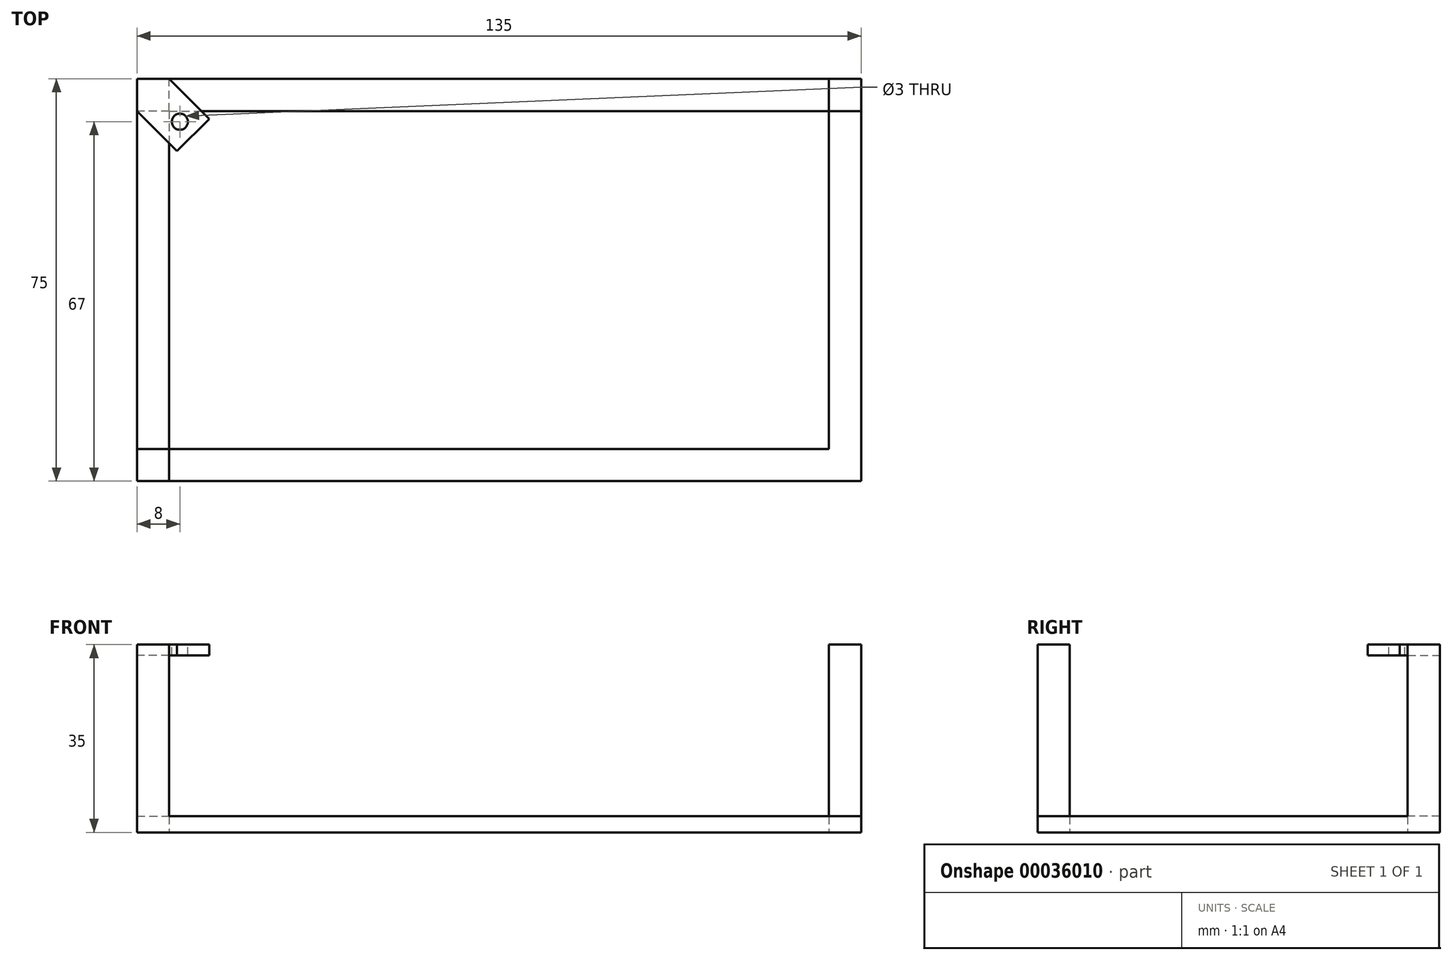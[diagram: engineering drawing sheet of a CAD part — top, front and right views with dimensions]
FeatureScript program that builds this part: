
annotation { "Feature Type Name" : "Feature", "Feature Type Description" : "" }
export const myFeature = defineFeature(function(context is Context, id is Id, definition is map)
    precondition{}
    {
        {
            var Q0;
            Q0=qCreatedBy(makeId("Top.planeOp"),FACE);
            var sketch = newSketch(context, id + "F0", { "sketchPlane" : qUnion([Q0])});
            skLineSegment(sketch, "E0.rect.bottom", {"start": v(-67.5, 37.5) * mm, "end": v(67.5, 37.5) * mm});
            skLineSegment(sketch, "E0.rect.top", {"start": v(-67.5, -37.5) * mm, "end": v(67.5, -37.5) * mm});
            skLineSegment(sketch, "E0.rect.left", {"start": v(-67.5, 37.5) * mm, "end": v(-67.5, -37.5) * mm});
            skLineSegment(sketch, "E0.rect.right", {"start": v(67.5, 37.5) * mm, "end": v(67.5, -37.5) * mm});
            skPoint(sketch, "E0.rect.middle", {"position": v(0, 0) * mm});
            skLineSegment(sketch, "E1.0", {"start": v(-61.5, 31.5) * mm, "end": v(61.5, 31.5) * mm});
            skLineSegment(sketch, "E1.1", {"start": v(-61.5, 31.5) * mm, "end": v(-61.5, -31.5) * mm});
            skLineSegment(sketch, "E1.2", {"start": v(-61.5, -31.5) * mm, "end": v(61.5, -31.5) * mm});
            skLineSegment(sketch, "E1.3", {"start": v(61.5, 31.5) * mm, "end": v(61.5, -31.5) * mm});
            skLineSegment(sketch, "E2.bottom", {"start": v(-61.5, 31.5) * mm, "end": v(-67.5, 31.5) * mm});
            skLineSegment(sketch, "E2.top", {"start": v(-61.5, 37.5) * mm, "end": v(-67.5, 37.5) * mm});
            skLineSegment(sketch, "E2.left", {"start": v(-61.5, 31.5) * mm, "end": v(-61.5, 37.5) * mm});
            skLineSegment(sketch, "E2.right", {"start": v(-67.5, 31.5) * mm, "end": v(-67.5, 37.5) * mm});
            skLineSegment(sketch, "E3.bottom", {"start": v(-61.5, -31.5) * mm, "end": v(-67.5, -31.5) * mm});
            skLineSegment(sketch, "E3.top", {"start": v(-61.5, -37.5) * mm, "end": v(-67.5, -37.5) * mm});
            skLineSegment(sketch, "E3.left", {"start": v(-61.5, -31.5) * mm, "end": v(-61.5, -37.5) * mm});
            skLineSegment(sketch, "E3.right", {"start": v(-67.5, -31.5) * mm, "end": v(-67.5, -37.5) * mm});
            skLineSegment(sketch, "E4.bottom", {"start": v(61.5, 31.5) * mm, "end": v(67.5, 31.5) * mm});
            skLineSegment(sketch, "E4.top", {"start": v(61.5, 37.5) * mm, "end": v(67.5, 37.5) * mm});
            skLineSegment(sketch, "E4.left", {"start": v(61.5, 31.5) * mm, "end": v(61.5, 37.5) * mm});
            skLineSegment(sketch, "E4.right", {"start": v(67.5, 31.5) * mm, "end": v(67.5, 37.5) * mm});
            skLineSegment(sketch, "E5.bottom", {"start": v(67.5, -37.5) * mm, "end": v(61.5, -37.5) * mm});
            skLineSegment(sketch, "E5.top", {"start": v(67.5, -31.5) * mm, "end": v(61.5, -31.5) * mm});
            skLineSegment(sketch, "E5.left", {"start": v(67.5, -37.5) * mm, "end": v(67.5, -31.5) * mm});
            skLineSegment(sketch, "E5.right", {"start": v(61.5, -37.5) * mm, "end": v(61.5, -31.5) * mm});
            skSolve(sketch);
        }
        {
            var Q0;
            Q0=makeQuery(id+"F0.imprint","IMPRINT",FACE,{"disambiguationData":[TD([[makeQuery(id+"F0.imprint","IMPRINT",EDGE,{"derivedFrom":sQuery(id+"F0.wireOp",EDGE,"E0.rect.bottom")}),-1.0]])]});
            var Q1;
            Q1=makeQuery(id+"F0.imprint","IMPRINT",FACE,{"disambiguationData":[TD([[makeQuery(id+"F0.imprint","IMPRINT",EDGE,{"derivedFrom":sQuery(id+"F0.wireOp",EDGE,"E0.rect.left")}),1.0]])]});
            var Q2;
            Q2=makeQuery(id+"F0.imprint","IMPRINT",FACE,{"disambiguationData":[TD([[makeQuery(id+"F0.imprint","IMPRINT",EDGE,{"derivedFrom":sQuery(id+"F0.wireOp",EDGE,"E3.bottom")}),1.0]])]});
            var Q3;
            Q3=makeQuery(id+"F0.imprint","IMPRINT",FACE,{"disambiguationData":[TD([[makeQuery(id+"F0.imprint","IMPRINT",EDGE,{"derivedFrom":sQuery(id+"F0.wireOp",EDGE,"E0.rect.top")}),1.0]])]});
            var Q4;
            Q4=makeQuery(id+"F0.imprint","IMPRINT",FACE,{"disambiguationData":[TD([[makeQuery(id+"F0.imprint","IMPRINT",EDGE,{"derivedFrom":sQuery(id+"F0.wireOp",EDGE,"E0.rect.right")}),-1.0]])]});
            var Q5;
            Q5=makeQuery(id+"F0.imprint","IMPRINT",FACE,{"disambiguationData":[TD([[makeQuery(id+"F0.imprint","IMPRINT",EDGE,{"derivedFrom":sQuery(id+"F0.wireOp",EDGE,"E5.bottom")}),-1.0]])]});
            var Q6;
            Q6=makeQuery(id+"F0.imprint","IMPRINT",FACE,{"disambiguationData":[TD([[makeQuery(id+"F0.imprint","IMPRINT",EDGE,{"derivedFrom":sQuery(id+"F0.wireOp",EDGE,"E4.bottom")}),1.0]])]});
            var Q7;
            Q7=makeQuery(id+"F0.imprint","IMPRINT",FACE,{"disambiguationData":[TD([[makeQuery(id+"F0.imprint","IMPRINT",EDGE,{"derivedFrom":sQuery(id+"F0.wireOp",EDGE,"E2.bottom")}),-1.0]])]});
            extrude(context, id + "F1", {"entities" : qUnion([Q0, Q1, Q2, Q3, Q4, Q5, Q6, Q7]), "depth" : 3 * mm});
        }
        {
            var Q0;
            Q0=makeQuery(id+"F0.imprint","IMPRINT",FACE,{"disambiguationData":[TD([[makeQuery(id+"F0.imprint","IMPRINT",EDGE,{"derivedFrom":sQuery(id+"F0.wireOp",EDGE,"E3.bottom")}),1.0]])]});
            var Q1;
            Q1=makeQuery(id+"F0.imprint","IMPRINT",FACE,{"disambiguationData":[TD([[makeQuery(id+"F0.imprint","IMPRINT",EDGE,{"derivedFrom":sQuery(id+"F0.wireOp",EDGE,"E5.bottom")}),-1.0]])]});
            var Q2;
            Q2=makeQuery(id+"F0.imprint","IMPRINT",FACE,{"disambiguationData":[TD([[makeQuery(id+"F0.imprint","IMPRINT",EDGE,{"derivedFrom":sQuery(id+"F0.wireOp",EDGE,"E4.bottom")}),1.0]])]});
            var Q3;
            Q3=makeQuery(id+"F0.imprint","IMPRINT",FACE,{"disambiguationData":[TD([[makeQuery(id+"F0.imprint","IMPRINT",EDGE,{"derivedFrom":sQuery(id+"F0.wireOp",EDGE,"E2.bottom")}),-1.0]])]});
            extrude(context, id + "F2", {"entities" : qUnion([Q0, Q1, Q2, Q3]), "operationType" : NewBodyOperationType.ADD, "depth" : 35 * mm});
        }
        {
            var Q0;
            Q0=makeQuery(id+"F2.opExtrude","CAP_FACE",FACE,{"disambiguationData":[OSD([sQuery(id+"F0.wireOp",EDGE,"E2.bottom"),sQuery(id+"F0.wireOp",EDGE,"E2.top"),sQuery(id+"F0.wireOp",EDGE,"E2.left"),sQuery(id+"F0.wireOp",EDGE,"E2.right")])],"isStart":false});
            var sketch = newSketch(context, id + "F3", { "sketchPlane" : qUnion([Q0])});
            skLineSegment(sketch, "E6", {"start": v(-67.5, 37.5) * mm, "end": v(-27.03, -2.97) * mm, "construction": true});
            skCircle(sketch, "E7", {"center": v(-59.5, 29.5) * mm, "radius": 1.5 * mm});
            skPoint(sketch, "E8", {"position": v(-64.5, 37.5) * mm});
            skLineSegment(sketch, "E9", {"start": v(-67.5, 31.5) * mm, "end": v(-60.03, 24.03) * mm});
            skLineSegment(sketch, "E10", {"start": v(-60.03, 24.03) * mm, "end": v(-54.03, 30.03) * mm});
            skLineSegment(sketch, "E11", {"start": v(-54.03, 30.03) * mm, "end": v(-61.5, 37.5) * mm});
            skLineSegment(sketch, "E12", {"start": v(-67.5, 31.5) * mm, "end": v(-61.5, 37.5) * mm});
            skSolve(sketch);
        }
        {
            var Q0;
            Q0=makeQuery(id+"F3.imprint","IMPRINT",FACE,{"disambiguationData":[TD([[makeQuery(id+"F3.imprint","IMPRINT",EDGE,{"derivedFrom":sQuery(id+"F3.wireOp",EDGE,"E7")}),-1.0]])]});
            extrude(context, id + "F4", {"entities" : qUnion([Q0]), "operationType" : NewBodyOperationType.ADD, "oppositeDirection" : true, "depth" : 2 * mm});
        }
    });
